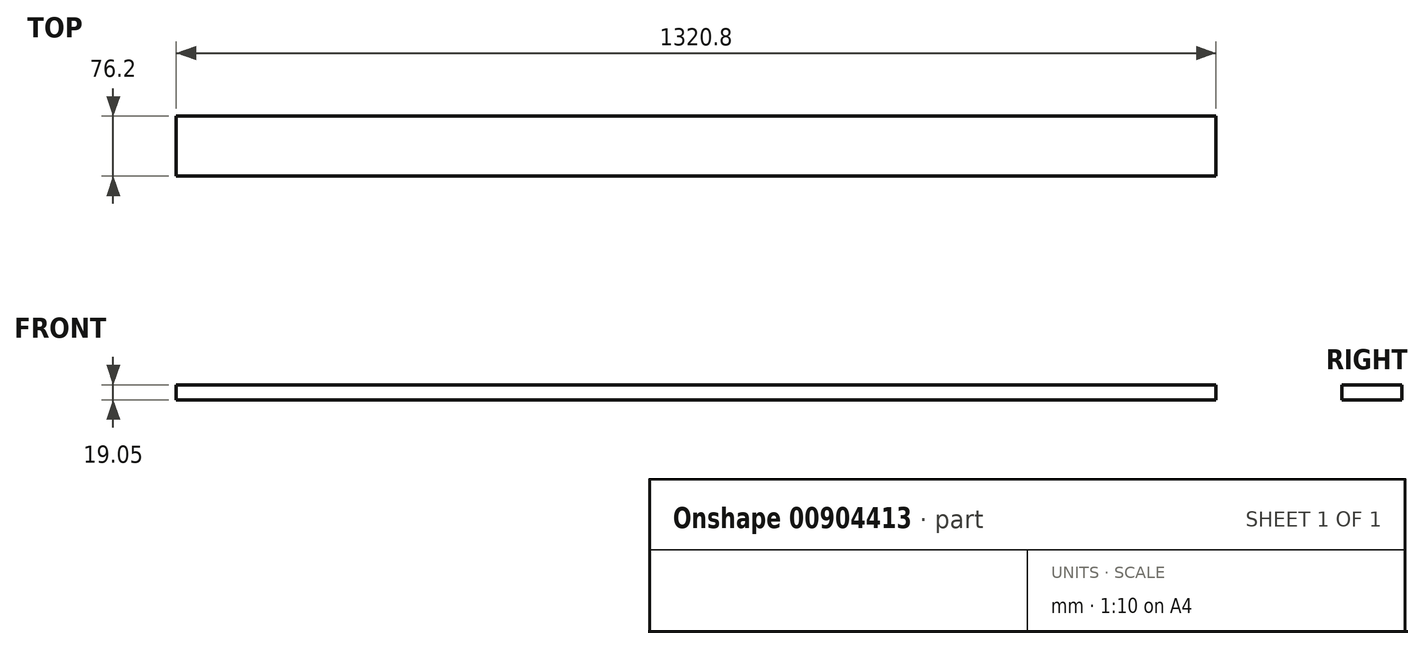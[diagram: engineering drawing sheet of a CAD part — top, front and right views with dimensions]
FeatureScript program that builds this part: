
annotation { "Feature Type Name" : "Feature", "Feature Type Description" : "" }
export const myFeature = defineFeature(function(context is Context, id is Id, definition is map)
    precondition{}
    {
        {
            var Q0;
            Q0=qCreatedBy(makeId("Top.planeOp"),FACE);
            var sketch = newSketch(context, id + "F0", { "sketchPlane" : qUnion([Q0])});
            skLineSegment(sketch, "E0.bottom", {"start": v(0, 0) * mm, "end": v(1320.8, 0) * mm});
            skLineSegment(sketch, "E0.top", {"start": v(0, 76.2) * mm, "end": v(1320.8, 76.2) * mm});
            skLineSegment(sketch, "E0.left", {"start": v(0, 0) * mm, "end": v(0, 76.2) * mm});
            skLineSegment(sketch, "E0.right", {"start": v(1320.8, 0) * mm, "end": v(1320.8, 76.2) * mm});
            skSolve(sketch);
        }
        {
            var Q0;
            Q0 = qSketchRegion(id + "F0", true);
            extrude(context, id + "F1", {"entities" : qUnion([Q0]), "depth" : 19.05 * mm, "offsetDistance" : 25.4 * mm});
        }
    });
